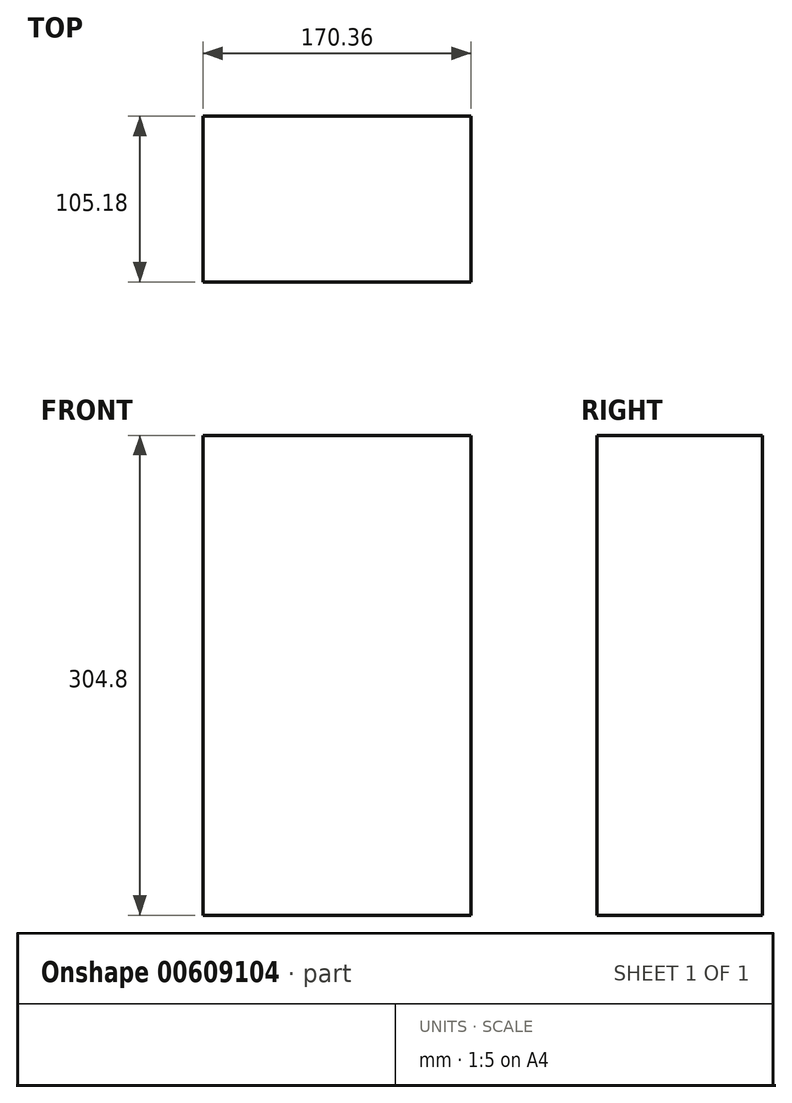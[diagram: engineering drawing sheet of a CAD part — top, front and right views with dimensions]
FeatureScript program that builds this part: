
annotation { "Feature Type Name" : "Feature", "Feature Type Description" : "" }
export const myFeature = defineFeature(function(context is Context, id is Id, definition is map)
    precondition{}
    {
        {
            var Q0;
            Q0=qCreatedBy(makeId("Top.planeOp"),FACE);
            var sketch = newSketch(context, id + "F0", { "sketchPlane" : qUnion([Q0])});
            skLineSegment(sketch, "E0.bottom", {"start": v(-85.18, 52.6) * mm, "end": v(85.18, 52.6) * mm});
            skLineSegment(sketch, "E0.top", {"start": v(-85.18, -52.6) * mm, "end": v(85.18, -52.6) * mm});
            skLineSegment(sketch, "E0.left", {"start": v(-85.18, 52.6) * mm, "end": v(-85.18, -52.6) * mm});
            skLineSegment(sketch, "E0.right", {"start": v(85.18, 52.6) * mm, "end": v(85.18, -52.6) * mm});
            skPoint(sketch, "E0.middle", {"position": v(0, 0) * mm});
            skSolve(sketch);
        }
        {
            var Q0;
            Q0=makeQuery(id+"F0.imprint","IMPRINT",FACE,{"disambiguationData":[TD([[makeQuery(id+"F0.imprint","IMPRINT",EDGE,{"derivedFrom":sQuery(id+"F0.wireOp",EDGE,"E0.bottom")}),-1.0]])]});
            extrude(context, id + "F1", {"entities" : qUnion([Q0]), "depth" : 304.8 * mm, "offsetDistance" : 25 * mm});
        }
    });
